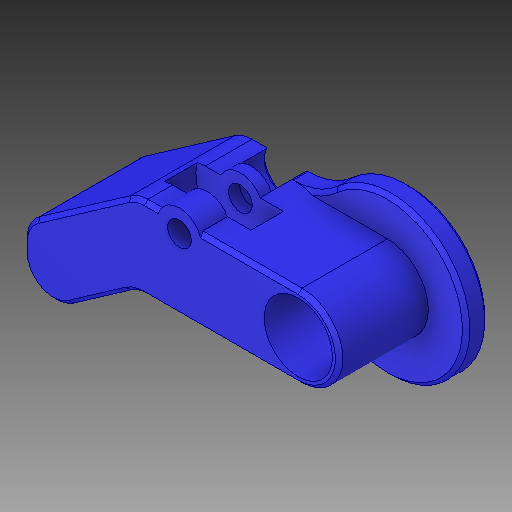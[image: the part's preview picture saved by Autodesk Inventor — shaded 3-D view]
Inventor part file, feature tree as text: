
AUTODESK INVENTOR PART (.ipt)
format: ipt  version: 2019 (Build 230136000, 136)  size: 515,072 bytes
history: native  units: mm
features: chamfer x1
ambient origin geometry x8: Origin, YZ Plane, XZ Plane, XY Plane, X Axis, Y Axis, Z Axis, Center Point
bodies: Solid1 (feature_tree)
feature tree (1):
  chamfer  "Chamfer3"  Distance=0.5mm Angle=45.0deg
